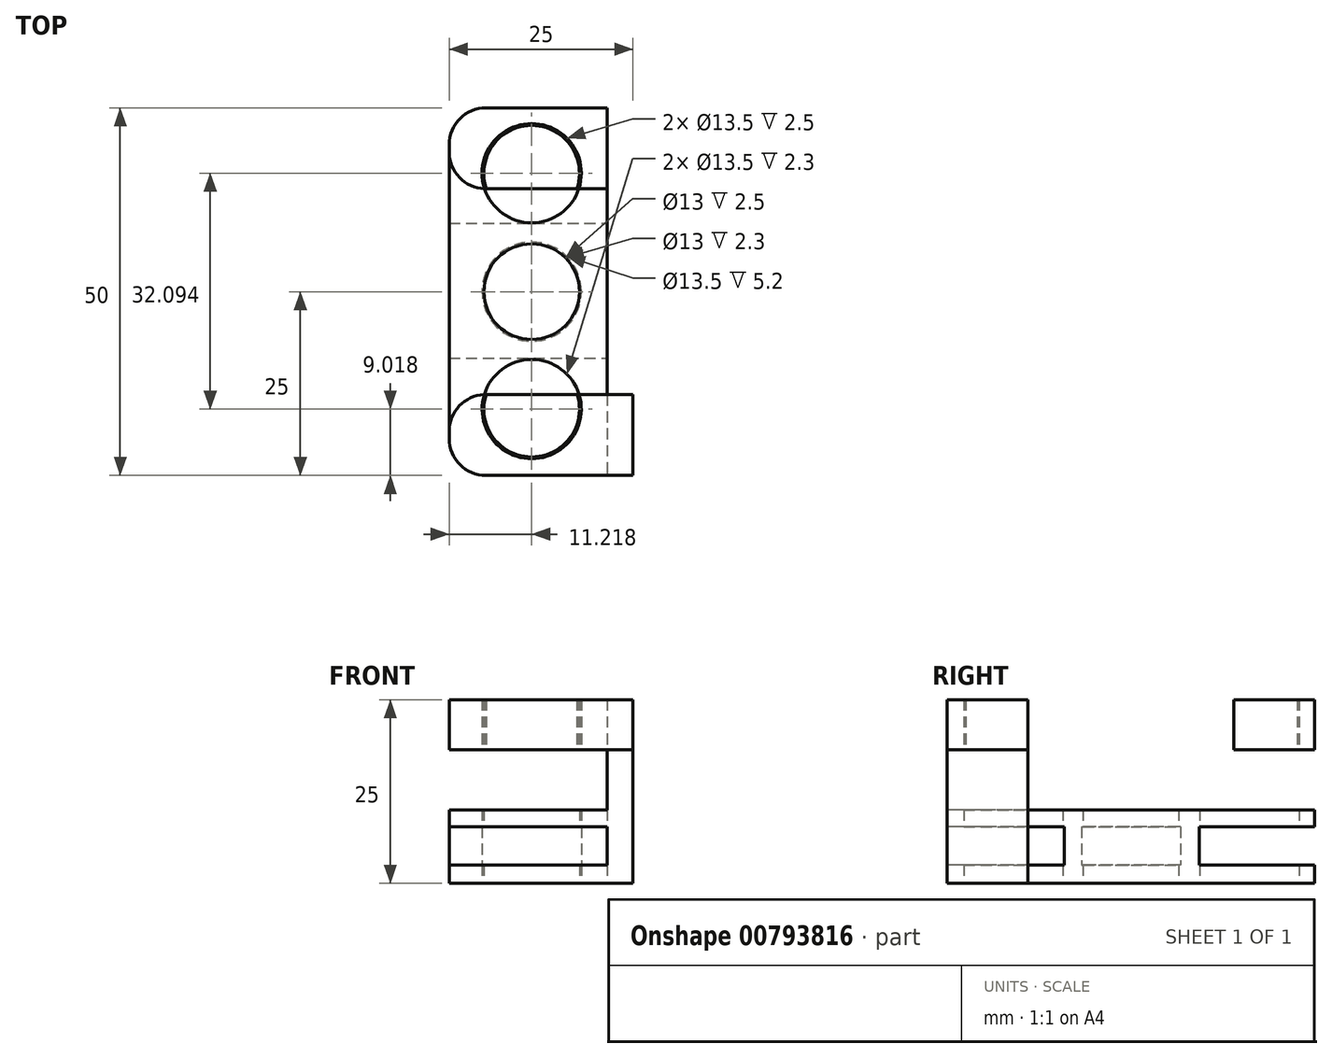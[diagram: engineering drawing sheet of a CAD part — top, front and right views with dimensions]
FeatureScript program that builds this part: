
annotation { "Feature Type Name" : "Feature", "Feature Type Description" : "" }
export const myFeature = defineFeature(function(context is Context, id is Id, definition is map)
    precondition{}
    {
        {
            var Q0;
            Q0=qCreatedBy(makeId("Top.planeOp"),FACE);
            var sketch = newSketch(context, id + "F0", { "sketchPlane" : qUnion([Q0])});
            skLineSegment(sketch, "E0.bottom", {"start": v(9.35, 14) * mm, "end": v(-15.65, 14) * mm});
            skLineSegment(sketch, "E0.top", {"start": v(9.35, -14) * mm, "end": v(-15.65, -14) * mm});
            skLineSegment(sketch, "E0.left", {"start": v(9.35, 14) * mm, "end": v(9.35, -14) * mm});
            skLineSegment(sketch, "E0.right", {"start": v(-15.65, 14) * mm, "end": v(-15.65, -14) * mm});
            skLineSegment(sketch, "E1.bottom", {"start": v(9.35, 4.6) * mm, "end": v(5.85, 4.6) * mm});
            skLineSegment(sketch, "E1.top", {"start": v(9.35, -4.6) * mm, "end": v(5.85, -4.6) * mm});
            skLineSegment(sketch, "E1.left", {"start": v(9.35, 4.6) * mm, "end": v(9.35, -4.6) * mm});
            skLineSegment(sketch, "E1.right", {"start": v(5.85, 4.6) * mm, "end": v(5.85, -4.6) * mm});
            skLineSegment(sketch, "E2.bottom", {"start": v(9.35, 14) * mm, "end": v(5.85, 14) * mm});
            skLineSegment(sketch, "E2.top", {"start": v(9.35, -14) * mm, "end": v(5.85, -14) * mm});
            skLineSegment(sketch, "E2.right", {"start": v(5.85, 14) * mm, "end": v(5.85, -14) * mm});
            skLineSegment(sketch, "E3", {"start": v(-4.65, 14) * mm, "end": v(-4.65, -14) * mm, "construction": true});
            skLineSegment(sketch, "E4.bottom", {"start": v(5.85, 25) * mm, "end": v(-15.65, 25) * mm});
            skLineSegment(sketch, "E4.top", {"start": v(5.85, -25) * mm, "end": v(-15.65, -25) * mm});
            skLineSegment(sketch, "E4.left", {"start": v(5.85, 25) * mm, "end": v(5.85, -25) * mm});
            skLineSegment(sketch, "E4.right", {"start": v(-15.65, 25) * mm, "end": v(-15.65, -25) * mm});
            skLineSegment(sketch, "E5.bottom", {"start": v(5.85, 14) * mm, "end": v(9.3, 14) * mm});
            skLineSegment(sketch, "E5.top", {"start": v(5.85, 25) * mm, "end": v(9.3, 25) * mm});
            skLineSegment(sketch, "E5.left", {"start": v(5.85, 14) * mm, "end": v(5.85, 25) * mm});
            skLineSegment(sketch, "E5.right", {"start": v(9.3, 14) * mm, "end": v(9.3, 25) * mm});
            skLineSegment(sketch, "E6.bottom", {"start": v(5.85, -25) * mm, "end": v(9.35, -25) * mm});
            skLineSegment(sketch, "E6.top", {"start": v(5.85, -14) * mm, "end": v(9.35, -14) * mm});
            skLineSegment(sketch, "E6.left", {"start": v(5.85, -25) * mm, "end": v(5.85, -14) * mm});
            skLineSegment(sketch, "E6.right", {"start": v(9.35, -25) * mm, "end": v(9.35, -14) * mm});
            skCircle(sketch, "E7", {"center": v(-4.43, -15.98) * mm, "radius": 6.5 * mm});
            skCircle(sketch, "E8", {"center": v(-4.43, 16.11) * mm, "radius": 6.5 * mm});
            skCircle(sketch, "E9", {"center": v(-4.43, 0) * mm, "radius": 6.5 * mm});
            skLineSegment(sketch, "E10", {"start": v(-15.65, 9.29) * mm, "end": v(5.85, 9.29) * mm});
            skLineSegment(sketch, "E11", {"start": v(-15.65, -9.05) * mm, "end": v(5.85, -9.05) * mm});
            skCircle(sketch, "E12", {"center": v(-4.43, -15.98) * mm, "radius": 6.75 * mm});
            skCircle(sketch, "E13", {"center": v(-4.43, 0) * mm, "radius": 6.75 * mm});
            skCircle(sketch, "E14", {"center": v(-4.43, 16.11) * mm, "radius": 6.75 * mm});
            skSolve(sketch);
        }
        {
            var Q0;
            {var subQ0=sQuery(id+"F0.wireOp",EDGE,"E4.right");var subQ1=sQuery(id+"F0.wireOp",EDGE,"E0.bottom");var subQ2=makeQuery(id+"F0.imprint","INTERSECT",VERTEX,{"derivedFrom":[subQ1,subQ0]});Q0=makeQuery(id+"F0.imprint","IMPRINT",FACE,{"disambiguationData":[TD([[makeQuery(id+"F0.imprint","IMPRINT",EDGE,{"disambiguationData":[TD([[subQ2,1.0]])],"derivedFrom":subQ1}),1.0]])]});}
            var Q1;
            {var subQ3=sQuery(id+"F0.wireOp",EDGE,"E4.bottom");Q1=makeQuery(id+"F0.imprint","IMPRINT",FACE,{"disambiguationData":[TD([[makeQuery(id+"F0.imprint","IMPRINT",EDGE,{"derivedFrom":subQ3}),1.0]])]});}
            var Q2;
            {var subQ0=sQuery(id+"F0.wireOp",EDGE,"E4.right");var subQ1=sQuery(id+"F0.wireOp",EDGE,"qjfhHtqs-ntaa-ZNBo-fZPD-U1VLx0ugnlIk");var subQ2=makeQuery(id+"F0.imprint","INTERSECT",VERTEX,{"disambiguationData":[OD(0.0)],"derivedFrom":[subQ1,subQ0]});Q2=makeQuery(id+"F0.imprint","IMPRINT",FACE,{"disambiguationData":[TD([[makeQuery(id+"F0.imprint","IMPRINT",EDGE,{"disambiguationData":[TD([[subQ2,1.0]])],"derivedFrom":subQ1}),1.0]])]});}
            var Q3;
            {var subQ0=sQuery(id+"F0.wireOp",EDGE,"E8");var subQ1=sQuery(id+"F0.wireOp",EDGE,"qjfhHtqs-ntaa-ZNBo-fZPD-U1VLx0ugnlIk");var subQ2=makeQuery(id+"F0.imprint","INTERSECT",VERTEX,{"disambiguationData":[OD(1.0)],"derivedFrom":[subQ1,subQ0]});Q3=makeQuery(id+"F0.imprint","IMPRINT",FACE,{"disambiguationData":[TD([[makeQuery(id+"F0.imprint","IMPRINT",EDGE,{"disambiguationData":[TD([[subQ2,1.0]])],"derivedFrom":subQ1}),-1.0]])]});}
            var Q4;
            {var subQ0=sQuery(id+"F0.wireOp",EDGE,"E4.right");var subQ1=sQuery(id+"F0.wireOp",EDGE,"E0.top");var subQ2=makeQuery(id+"F0.imprint","INTERSECT",VERTEX,{"derivedFrom":[subQ1,subQ0]});Q4=makeQuery(id+"F0.imprint","IMPRINT",FACE,{"disambiguationData":[TD([[makeQuery(id+"F0.imprint","IMPRINT",EDGE,{"disambiguationData":[TD([[subQ2,1.0]])],"derivedFrom":subQ1}),-1.0]])]});}
            var Q5;
            Q5=makeQuery(id+"F0.imprint","IMPRINT",FACE,{"disambiguationData":[TD([[makeQuery(id+"F0.imprint","IMPRINT",EDGE,{"derivedFrom":sQuery(id+"F0.wireOp",EDGE,"E9")}),-1.0]])]});
            var Q6;
            {var subQ3=sQuery(id+"F0.wireOp",EDGE,"E4.top");Q6=makeQuery(id+"F0.imprint","IMPRINT",FACE,{"disambiguationData":[TD([[makeQuery(id+"F0.imprint","IMPRINT",EDGE,{"derivedFrom":subQ3}),-1.0]])]});}
            var Q7;
            {var subQ0=sQuery(id+"F0.wireOp",EDGE,"E12");var subQ1=sQuery(id+"F0.wireOp",EDGE,"E0.top");var subQ2=makeQuery(id+"F0.imprint","INTERSECT",VERTEX,{"disambiguationData":[OD(0.0)],"derivedFrom":[subQ1,subQ0]});Q7=makeQuery(id+"F0.imprint","IMPRINT",FACE,{"disambiguationData":[TD([[makeQuery(id+"F0.imprint","IMPRINT",EDGE,{"disambiguationData":[TD([[subQ2,-1.0]])],"derivedFrom":subQ1}),-1.0]])]});}
            var Q8;
            {var subQ0=sQuery(id+"F0.wireOp",EDGE,"E12");var subQ1=sQuery(id+"F0.wireOp",EDGE,"E0.top");var subQ2=makeQuery(id+"F0.imprint","INTERSECT",VERTEX,{"disambiguationData":[OD(0.0)],"derivedFrom":[subQ1,subQ0]});Q8=makeQuery(id+"F0.imprint","IMPRINT",FACE,{"disambiguationData":[TD([[makeQuery(id+"F0.imprint","IMPRINT",EDGE,{"disambiguationData":[TD([[subQ2,-1.0]])],"derivedFrom":subQ1}),1.0]])]});}
            var Q9;
            {var subQ3=sQuery(id+"F0.wireOp",EDGE,"E10");Q9=makeQuery(id+"F0.imprint","IMPRINT",FACE,{"disambiguationData":[TD([[makeQuery(id+"F0.imprint","IMPRINT",EDGE,{"derivedFrom":subQ3}),-1.0]])]});}
            var Q10;
            {var subQ0=sQuery(id+"F0.wireOp",EDGE,"E14");var subQ1=sQuery(id+"F0.wireOp",EDGE,"E0.bottom");var subQ2=makeQuery(id+"F0.imprint","INTERSECT",VERTEX,{"disambiguationData":[OD(0.0)],"derivedFrom":[subQ1,subQ0]});Q10=makeQuery(id+"F0.imprint","IMPRINT",FACE,{"disambiguationData":[TD([[makeQuery(id+"F0.imprint","IMPRINT",EDGE,{"disambiguationData":[TD([[subQ2,-1.0]])],"derivedFrom":subQ1}),1.0]])]});}
            var Q11;
            {var subQ0=sQuery(id+"F0.wireOp",EDGE,"E14");var subQ1=sQuery(id+"F0.wireOp",EDGE,"E0.bottom");var subQ2=makeQuery(id+"F0.imprint","INTERSECT",VERTEX,{"disambiguationData":[OD(0.0)],"derivedFrom":[subQ1,subQ0]});Q11=makeQuery(id+"F0.imprint","IMPRINT",FACE,{"disambiguationData":[TD([[makeQuery(id+"F0.imprint","IMPRINT",EDGE,{"disambiguationData":[TD([[subQ2,-1.0]])],"derivedFrom":subQ1}),-1.0]])]});}
            extrude(context, id + "F1", {"entities" : qUnion([Q0, Q1, Q2, Q3, Q4, Q5, Q6, Q7, Q8, Q9, Q10, Q11]), "depth" : 10 * mm, "offsetDistance" : 25 * mm});
        }
        {
            var Q0;
            {var subQ3=sQuery(id+"F0.wireOp",EDGE,"E5.bottom");Q0=makeQuery(id+"F0.imprint","IMPRINT",FACE,{"disambiguationData":[TD([[makeQuery(id+"F0.imprint","IMPRINT",EDGE,{"derivedFrom":subQ3}),1.0]])]});}
            var Q1;
            Q1=makeQuery(id+"F0.imprint","IMPRINT",FACE,{"disambiguationData":[TD([[makeQuery(id+"F0.imprint","IMPRINT",EDGE,{"derivedFrom":sQuery(id+"F0.wireOp",EDGE,"E6.bottom")}),1.0]])]});
            extrude(context, id + "F2", {"entities" : qUnion([Q0, Q1]), "operationType" : NewBodyOperationType.ADD, "depth" : 18.2 * mm, "offsetDistance" : 25 * mm});
        }
        {
            var Q0;
            Q0=makeQuery(id+"F1.opExtrude","SWEPT_EDGE",EDGE,{"disambiguationData":[OSD([sQuery(id+"F0.wireOp",EDGE,"E4.top"),sQuery(id+"F0.wireOp",EDGE,"E4.right")])]});
            var Q1;
            Q1=makeQuery(id+"F1.opExtrude","SWEPT_EDGE",EDGE,{"disambiguationData":[OSD([sQuery(id+"F0.wireOp",EDGE,"E4.bottom"),sQuery(id+"F0.wireOp",EDGE,"E4.right")])]});
            fillet(context, id + "F3", {"entities" : qUnion([Q0, Q1]), "radius" : 5 * mm, "tangentPropagation" : true, "allowEdgeOverflow" : false});
        }
        {
            var Q0;
            {var subQ0=sQuery(id+"F0.wireOp",EDGE,"E12");var subQ1=sQuery(id+"F0.wireOp",EDGE,"E0.top");var subQ2=makeQuery(id+"F0.imprint","INTERSECT",VERTEX,{"disambiguationData":[OD(0.0)],"derivedFrom":[subQ1,subQ0]});Q0=makeQuery(id+"F0.imprint","IMPRINT",FACE,{"disambiguationData":[TD([[makeQuery(id+"F0.imprint","IMPRINT",EDGE,{"disambiguationData":[TD([[subQ2,-1.0]])],"derivedFrom":subQ1}),1.0]])]});}
            var Q1;
            {var subQ0=sQuery(id+"F0.wireOp",EDGE,"E12");var subQ1=sQuery(id+"F0.wireOp",EDGE,"E0.top");var subQ2=makeQuery(id+"F0.imprint","INTERSECT",VERTEX,{"disambiguationData":[OD(0.0)],"derivedFrom":[subQ1,subQ0]});Q1=makeQuery(id+"F0.imprint","IMPRINT",FACE,{"disambiguationData":[TD([[makeQuery(id+"F0.imprint","IMPRINT",EDGE,{"disambiguationData":[TD([[subQ2,-1.0]])],"derivedFrom":subQ1}),-1.0]])]});}
            var Q2;
            Q2=makeQuery(id+"F0.imprint","IMPRINT",FACE,{"disambiguationData":[TD([[makeQuery(id+"F0.imprint","IMPRINT",EDGE,{"derivedFrom":sQuery(id+"F0.wireOp",EDGE,"E9")}),-1.0]])]});
            var Q3;
            {var subQ0=sQuery(id+"F0.wireOp",EDGE,"E14");var subQ1=sQuery(id+"F0.wireOp",EDGE,"E0.bottom");var subQ2=makeQuery(id+"F0.imprint","INTERSECT",VERTEX,{"disambiguationData":[OD(0.0)],"derivedFrom":[subQ1,subQ0]});Q3=makeQuery(id+"F0.imprint","IMPRINT",FACE,{"disambiguationData":[TD([[makeQuery(id+"F0.imprint","IMPRINT",EDGE,{"disambiguationData":[TD([[subQ2,-1.0]])],"derivedFrom":subQ1}),1.0]])]});}
            var Q4;
            {var subQ0=sQuery(id+"F0.wireOp",EDGE,"E14");var subQ1=sQuery(id+"F0.wireOp",EDGE,"E0.bottom");var subQ2=makeQuery(id+"F0.imprint","INTERSECT",VERTEX,{"disambiguationData":[OD(0.0)],"derivedFrom":[subQ1,subQ0]});Q4=makeQuery(id+"F0.imprint","IMPRINT",FACE,{"disambiguationData":[TD([[makeQuery(id+"F0.imprint","IMPRINT",EDGE,{"disambiguationData":[TD([[subQ2,-1.0]])],"derivedFrom":subQ1}),-1.0]])]});}
            extrude(context, id + "F4", {"entities" : qUnion([Q0, Q1, Q2, Q3, Q4]), "operationType" : NewBodyOperationType.REMOVE, "depth" : 7.7 * mm, "offsetDistance" : 25 * mm, "hasSecondDirection" : true, "secondDirectionOppositeDirection" : false, "secondDirectionDepth" : 2.5 * mm});
        }
        {
            var Q0;
            {var subQ0=sQuery(id+"F0.wireOp",EDGE,"E12");var subQ1=sQuery(id+"F0.wireOp",EDGE,"E0.top");var subQ2=makeQuery(id+"F0.imprint","INTERSECT",VERTEX,{"disambiguationData":[OD(0.0)],"derivedFrom":[subQ1,subQ0]});Q0=makeQuery(id+"F0.imprint","IMPRINT",FACE,{"disambiguationData":[TD([[makeQuery(id+"F0.imprint","IMPRINT",EDGE,{"disambiguationData":[TD([[subQ2,-1.0]])],"derivedFrom":subQ1}),1.0]])]});}
            var Q1;
            {var subQ0=sQuery(id+"F0.wireOp",EDGE,"E7");var subQ1=sQuery(id+"F0.wireOp",EDGE,"E0.top");var subQ2=makeQuery(id+"F0.imprint","INTERSECT",VERTEX,{"disambiguationData":[OD(0.0)],"derivedFrom":[subQ1,subQ0]});Q1=makeQuery(id+"F0.imprint","IMPRINT",FACE,{"disambiguationData":[TD([[makeQuery(id+"F0.imprint","IMPRINT",EDGE,{"disambiguationData":[TD([[subQ2,-1.0]])],"derivedFrom":subQ1}),1.0]])]});}
            var Q2;
            {var subQ3=sQuery(id+"F0.wireOp",EDGE,"E4.top");Q2=makeQuery(id+"F0.imprint","IMPRINT",FACE,{"disambiguationData":[TD([[makeQuery(id+"F0.imprint","IMPRINT",EDGE,{"derivedFrom":subQ3}),-1.0]])]});}
            var Q3;
            Q3=makeQuery(id+"F0.imprint","IMPRINT",FACE,{"disambiguationData":[TD([[makeQuery(id+"F0.imprint","IMPRINT",EDGE,{"derivedFrom":sQuery(id+"F0.wireOp",EDGE,"E6.bottom")}),1.0]])]});
            var Q4;
            {var subQ3=sQuery(id+"F0.wireOp",EDGE,"E5.bottom");Q4=makeQuery(id+"F0.imprint","IMPRINT",FACE,{"disambiguationData":[TD([[makeQuery(id+"F0.imprint","IMPRINT",EDGE,{"derivedFrom":subQ3}),1.0]])]});}
            var Q5;
            {var subQ3=sQuery(id+"F0.wireOp",EDGE,"E4.bottom");Q5=makeQuery(id+"F0.imprint","IMPRINT",FACE,{"disambiguationData":[TD([[makeQuery(id+"F0.imprint","IMPRINT",EDGE,{"derivedFrom":subQ3}),1.0]])]});}
            var Q6;
            {var subQ0=sQuery(id+"F0.wireOp",EDGE,"E8");var subQ1=sQuery(id+"F0.wireOp",EDGE,"E0.bottom");var subQ2=makeQuery(id+"F0.imprint","INTERSECT",VERTEX,{"disambiguationData":[OD(0.0)],"derivedFrom":[subQ1,subQ0]});Q6=makeQuery(id+"F0.imprint","IMPRINT",FACE,{"disambiguationData":[TD([[makeQuery(id+"F0.imprint","IMPRINT",EDGE,{"disambiguationData":[TD([[subQ2,-1.0]])],"derivedFrom":subQ1}),-1.0]])]});}
            var Q7;
            {var subQ0=sQuery(id+"F0.wireOp",EDGE,"E14");var subQ1=sQuery(id+"F0.wireOp",EDGE,"E0.bottom");var subQ2=makeQuery(id+"F0.imprint","INTERSECT",VERTEX,{"disambiguationData":[OD(0.0)],"derivedFrom":[subQ1,subQ0]});Q7=makeQuery(id+"F0.imprint","IMPRINT",FACE,{"disambiguationData":[TD([[makeQuery(id+"F0.imprint","IMPRINT",EDGE,{"disambiguationData":[TD([[subQ2,-1.0]])],"derivedFrom":subQ1}),-1.0]])]});}
            extrude(context, id + "F5", {"entities" : qUnion([Q0, Q1, Q2, Q3, Q4, Q5, Q6, Q7]), "depth" : 25 * mm, "offsetDistance" : 25 * mm, "hasSecondDirection" : true, "secondDirectionOppositeDirection" : false, "secondDirectionDepth" : 18.2 * mm});
        }
        {
            var Q0;
            Q0=makeQuery(id+"F5.opExtrude","SWEPT_EDGE",EDGE,{"disambiguationData":[OSD([sQuery(id+"F0.wireOp",EDGE,"E4.bottom"),sQuery(id+"F0.wireOp",EDGE,"E4.right")])]});
            var Q1;
            Q1=makeQuery(id+"F5.opExtrude","SWEPT_EDGE",EDGE,{"disambiguationData":[OSD([sQuery(id+"F0.wireOp",EDGE,"E4.top"),sQuery(id+"F0.wireOp",EDGE,"E4.right")])]});
            var Q2;
            Q2=makeQuery(id+"F5.opExtrude","SWEPT_EDGE",EDGE,{"disambiguationData":[OSD([sQuery(id+"F0.wireOp",EDGE,"E0.top"),sQuery(id+"F0.wireOp",EDGE,"E4.right")])]});
            var Q3;
            Q3=makeQuery(id+"F5.opExtrude","SWEPT_EDGE",EDGE,{"disambiguationData":[OSD([sQuery(id+"F0.wireOp",EDGE,"E0.bottom"),sQuery(id+"F0.wireOp",EDGE,"E4.right")])]});
            fillet(context, id + "F6", {"entities" : qUnion([Q0, Q1, Q2, Q3]), "radius" : 5 * mm, "tangentPropagation" : true, "allowEdgeOverflow" : false});
        }
    });
